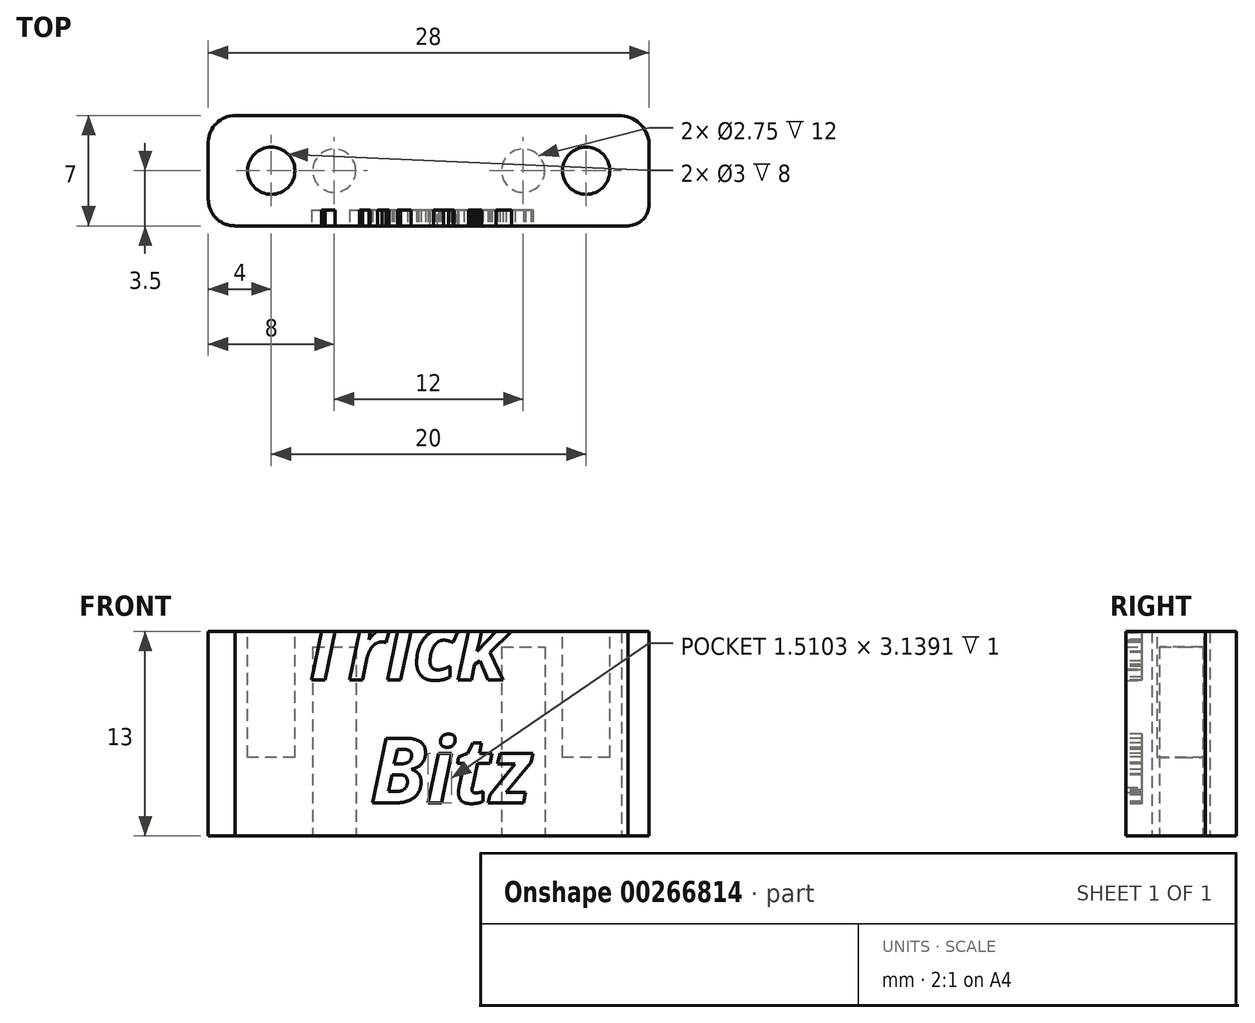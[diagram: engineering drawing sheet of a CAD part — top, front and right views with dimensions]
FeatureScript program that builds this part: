
annotation { "Feature Type Name" : "Feature", "Feature Type Description" : "" }
export const myFeature = defineFeature(function(context is Context, id is Id, definition is map)
    precondition{}
    {
        {
            var Q0;
            Q0=qCreatedBy(makeId("Top.planeOp"),FACE);
            var sketch = newSketch(context, id + "F0", { "sketchPlane" : qUnion([Q0])});
            skLineSegment(sketch, "E0.bottom", {"start": v(-26.34, 0) * mm, "end": v(-1.34, 0) * mm});
            skLineSegment(sketch, "E0.top", {"start": v(-26.3, 7) * mm, "end": v(-1.76, 7) * mm});
            skLineSegment(sketch, "E0.left", {"start": v(-28, 1.66) * mm, "end": v(-28, 5.32) * mm});
            skLineSegment(sketch, "E0.right", {"start": v(0, 1.37) * mm, "end": v(0, 5.15) * mm});
            skArc(sketch, "E1", {"start": v(-26.3, 7) * mm, "mid": v(-27.49, 6.5) * mm, "end": v(-28, 5.32) * mm});
            skArc(sketch, "E2", {"start": v(-28, 1.66) * mm, "mid": v(-27.5, 0.48) * mm, "end": v(-26.3, 0) * mm});
            skPoint(sketch, "E3.orphan", {"position": v(-28, 7) * mm});
            skPoint(sketch, "E4.orphan", {"position": v(-28, 0) * mm});
            skArc(sketch, "E5", {"start": v(0, 5.04) * mm, "mid": v(-0.49, 6.37) * mm, "end": v(-1.76, 7) * mm});
            skPoint(sketch, "E6.orphan", {"position": v(0, 7) * mm});
            skArc(sketch, "E7", {"start": v(-1.34, 0) * mm, "mid": v(-0.4, 0.41) * mm, "end": v(0, 1.37) * mm});
            skSolve(sketch);
        }
        {
            var Q0;
            Q0 = qSketchRegion(id + "F0", true);
            extrude(context, id + "F1", {"entities" : qUnion([Q0]), "depth" : 13 * mm});
        }
        {
            var Q0;
            Q0=makeQuery(id+"F1.opExtrude","CAP_FACE",FACE,{"disambiguationData":[OSD([sQuery(id+"F0.wireOp",EDGE,"E0.bottom"),sQuery(id+"F0.wireOp",EDGE,"E0.top"),sQuery(id+"F0.wireOp",EDGE,"E0.left"),sQuery(id+"F0.wireOp",EDGE,"E0.right"),sQuery(id+"F0.wireOp",EDGE,"E1"),sQuery(id+"F0.wireOp",EDGE,"E2"),sQuery(id+"F0.wireOp",EDGE,"E5"),sQuery(id+"F0.wireOp",EDGE,"E7")])],"isStart":true});
            var sketch = newSketch(context, id + "F2", { "sketchPlane" : qUnion([Q0])});
            skCircle(sketch, "E8", {"center": v(-20, -3.5) * mm, "radius": 1.38 * mm});
            skCircle(sketch, "E9", {"center": v(-8, -3.5) * mm, "radius": 1.38 * mm});
            skSolve(sketch);
        }
        {
            var Q0;
            Q0=makeQuery(id+"F2.imprint","IMPRINT",FACE,{"disambiguationData":[TD([[makeQuery(id+"F2.imprint","IMPRINT",EDGE,{"derivedFrom":sQuery(id+"F2.wireOp",EDGE,"E8")}),1.0]])]});
            var Q1;
            Q1=makeQuery(id+"F2.imprint","IMPRINT",FACE,{"disambiguationData":[TD([[makeQuery(id+"F2.imprint","IMPRINT",EDGE,{"derivedFrom":sQuery(id+"F2.wireOp",EDGE,"E9")}),1.0]])]});
            extrude(context, id + "F3", {"entities" : qUnion([Q0, Q1]), "operationType" : NewBodyOperationType.REMOVE, "oppositeDirection" : true, "depth" : 10 * mm});
        }
        {
            var Q0;
            Q0=makeQuery(id+"F1.opExtrude","CAP_FACE",FACE,{"disambiguationData":[OSD([sQuery(id+"F0.wireOp",EDGE,"E0.bottom"),sQuery(id+"F0.wireOp",EDGE,"E0.top"),sQuery(id+"F0.wireOp",EDGE,"E0.left"),sQuery(id+"F0.wireOp",EDGE,"E0.right"),sQuery(id+"F0.wireOp",EDGE,"E1"),sQuery(id+"F0.wireOp",EDGE,"E2"),sQuery(id+"F0.wireOp",EDGE,"E5"),sQuery(id+"F0.wireOp",EDGE,"E7")])],"isStart":false});
            var sketch = newSketch(context, id + "F4", { "sketchPlane" : qUnion([Q0])});
            skCircle(sketch, "E10", {"center": v(-24, 3.5) * mm, "radius": 1.5 * mm});
            skCircle(sketch, "E11", {"center": v(-4, 3.5) * mm, "radius": 1.5 * mm});
            skSolve(sketch);
        }
        {
            var Q0;
            Q0 = qSketchRegion(id + "F4", true);
            extrude(context, id + "F5", {"entities" : qUnion([Q0]), "operationType" : NewBodyOperationType.REMOVE, "oppositeDirection" : true, "depth" : 10 * mm});
        }
        {
            var Q0;
            Q0=makeQuery(id+"F1.opExtrude","CAP_FACE",FACE,{"disambiguationData":[OSD([sQuery(id+"F0.wireOp",EDGE,"E0.bottom"),sQuery(id+"F0.wireOp",EDGE,"E0.top"),sQuery(id+"F0.wireOp",EDGE,"E0.left"),sQuery(id+"F0.wireOp",EDGE,"E0.right"),sQuery(id+"F0.wireOp",EDGE,"E1"),sQuery(id+"F0.wireOp",EDGE,"E2"),sQuery(id+"F0.wireOp",EDGE,"E5"),sQuery(id+"F0.wireOp",EDGE,"E7")])],"isStart":true});
            extrude(context, id + "F6", {"entities" : qUnion([Q0]), "operationType" : NewBodyOperationType.ADD, "depth" : 2 * mm});
        }
        {
            var Q0;
            {var subQ0=sQuery(id+"F0.wireOp",EDGE,"E0.bottom");Q0=makeQuery(id+"F6.boolean.opBoolean","MERGE",FACE,{"derivedFrom":[makeQuery(id+"F1.opExtrude","SWEPT_FACE",FACE,{"disambiguationData":[OSD([subQ0])]}),makeQuery(id+"F6.opExtrude","SWEPT_FACE",FACE,{"disambiguationData":[OSD([subQ0])]})]});}
            var sketch = newSketch(context, id + "F7", { "sketchPlane" : qUnion([Q0])});
            skText(sketch, "E12", { "text": "Trick\n   Bitz", "fontName": "OpenSans-BoldItalic.ttf"});
            const initialGuessF7  = {"E12": [-0.0222, 0.00792, 1, 0, 0.00414]};
            skSetInitialGuess(sketch, initialGuessF7);
            skSolve(sketch);
        }
        {
            var Q0;
            Q0 = qSketchRegion(id + "F7", true);
            extrude(context, id + "F8", {"entities" : qUnion([Q0]), "operationType" : NewBodyOperationType.REMOVE, "oppositeDirection" : true, "depth" : 1 * mm});
        }
        {
            var Q0;
            Q0=makeQuery(id+"F1.opExtrude","CAP_FACE",FACE,{"disambiguationData":[OSD([sQuery(id+"F0.wireOp",EDGE,"E0.bottom"),sQuery(id+"F0.wireOp",EDGE,"E0.top"),sQuery(id+"F0.wireOp",EDGE,"E0.left"),sQuery(id+"F0.wireOp",EDGE,"E0.right"),sQuery(id+"F0.wireOp",EDGE,"E1"),sQuery(id+"F0.wireOp",EDGE,"E2"),sQuery(id+"F0.wireOp",EDGE,"E5"),sQuery(id+"F0.wireOp",EDGE,"E7")])],"isStart":false});
            extrude(context, id + "F9", {"entities" : qUnion([Q0]), "operationType" : NewBodyOperationType.REMOVE, "oppositeDirection" : true, "depth" : 2 * mm, "offsetDistance" : 25 * mm});
        }
    });
